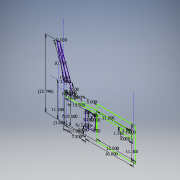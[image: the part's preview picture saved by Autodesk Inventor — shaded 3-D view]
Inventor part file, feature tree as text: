
AUTODESK INVENTOR PART (.ipt)
format: ipt  version: 2017 SP1 (Build 210196100, 196)  size: 141,824 bytes
history: native  units: in
note: dims shown in document units (in); Inventor stores cm internally (conversion verified against a paired STEP export)
features: sketch x1
ambient origin geometry x8: Origin, YZ Plane, XZ Plane, XY Plane, X Axis, Y Axis, Z Axis, Center Point
feature tree (1):
  sketch  "Sketch1"  dims[d0=2.5in d1=5.0in d2=1.25in d3=0.75in d4=16.0in d7=5.0in d8=8.0in d9=5.0in d10=10.5in d11=0.25in d12=13.0in d13=11.0in d14=3.0in d17=3.5in d19=2.0in d20=11.0in d22=1.25in d23=4.0in d24=1.0in d25=7.5in d30=1.0in d31=4.5in d34=11.5in d36=1.0in d38=1.2in d39=1.5in d40=9.5in d41=7.0in d42=5.0in d44=1.0in d45=10.75in d46=3.5in d51=15.0deg d52=2.749in d53=2.7461in d57=1.6823in d58=22.7456in d59=0.125in]
